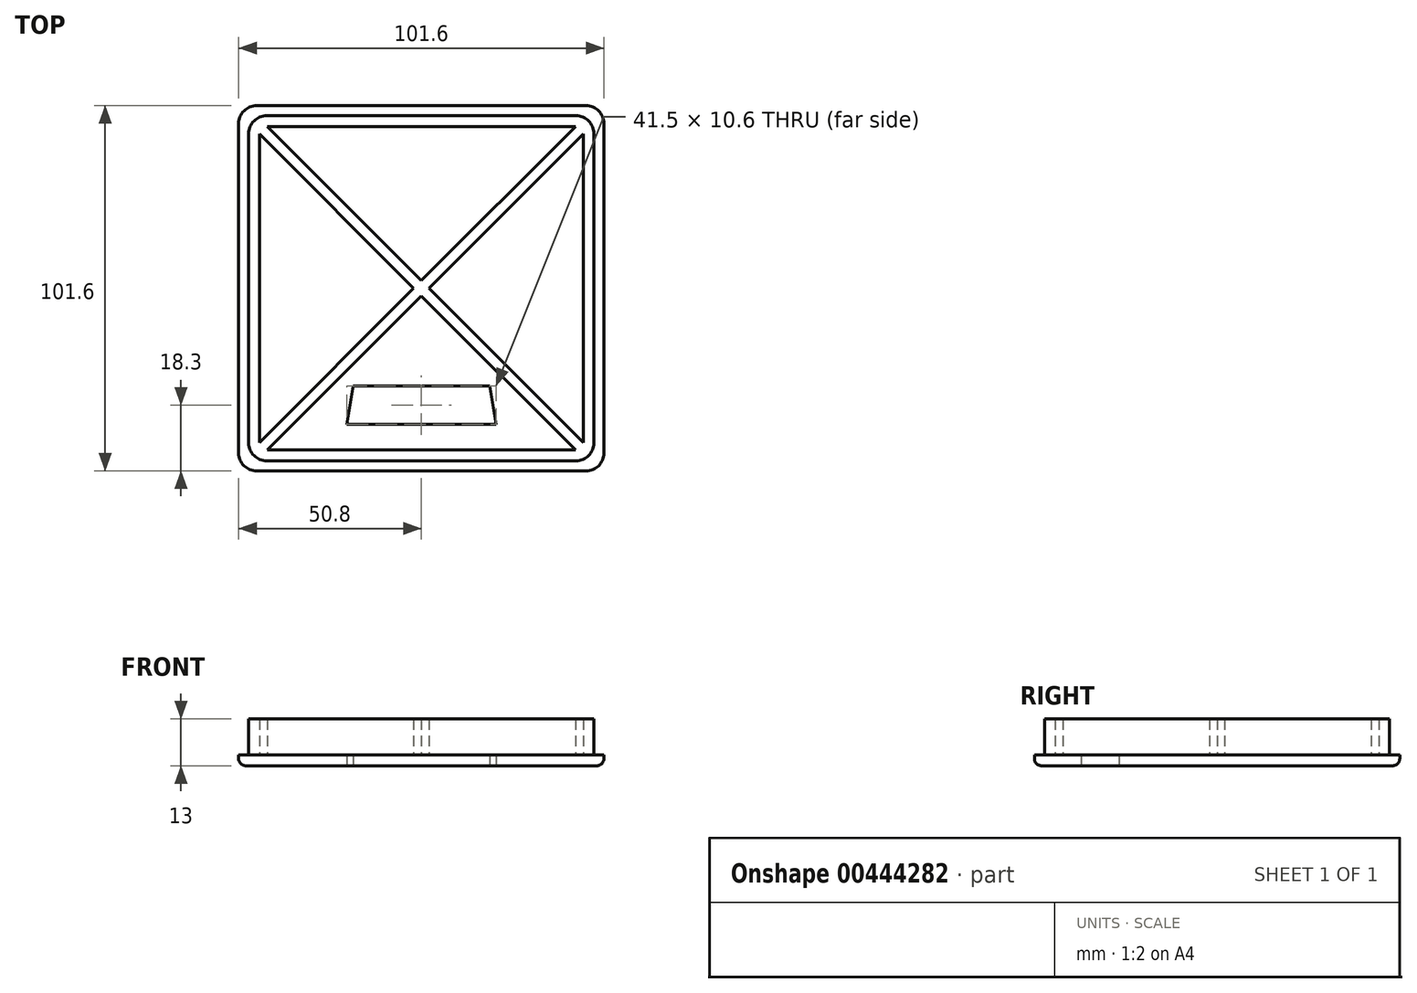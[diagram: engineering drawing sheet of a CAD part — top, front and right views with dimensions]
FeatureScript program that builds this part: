
annotation { "Feature Type Name" : "Feature", "Feature Type Description" : "" }
export const myFeature = defineFeature(function(context is Context, id is Id, definition is map)
    precondition{}
    {
        {
            assignVariable(context, id + "F0", {"name" : "thickness", "anyValue" : 3});
        }
        {
            var Q0;
            Q0=qCreatedBy(makeId("Top.planeOp"),FACE);
            var sketch = newSketch(context, id + "F1", { "sketchPlane" : qUnion([Q0])});
            skLineSegment(sketch, "E0.bottom", {"start": v(45, -45) * mm, "end": v(-45, -45) * mm});
            skLineSegment(sketch, "E0.top", {"start": v(45, 45) * mm, "end": v(-45, 45) * mm});
            skLineSegment(sketch, "E0.left", {"start": v(45, -45) * mm, "end": v(45, 45) * mm});
            skLineSegment(sketch, "E0.right", {"start": v(-45, -45) * mm, "end": v(-45, 45) * mm});
            skPoint(sketch, "E0.middle", {"position": v(0, 0) * mm});
            skLineSegment(sketch, "E1.bottom", {"start": v(-43, 48) * mm, "end": v(43, 48) * mm});
            skLineSegment(sketch, "E1.top", {"start": v(-43, -48) * mm, "end": v(43, -48) * mm});
            skLineSegment(sketch, "E1.left", {"start": v(-48, 43) * mm, "end": v(-48, -43) * mm});
            skLineSegment(sketch, "E1.right", {"start": v(48, 43) * mm, "end": v(48, -43) * mm});
            skLineSegment(sketch, "E2", {"start": v(-45, 45) * mm, "end": v(45, -45) * mm, "construction": true});
            skLineSegment(sketch, "E3", {"start": v(45, 45) * mm, "end": v(-45, -45) * mm, "construction": true});
            skLineSegment(sketch, "E4.bottom", {"start": v(-2.12, 2.12) * mm, "end": v(2.12, 2.12) * mm, "construction": true});
            skLineSegment(sketch, "E4.top", {"start": v(-2.12, -2.12) * mm, "end": v(2.12, -2.12) * mm, "construction": true});
            skLineSegment(sketch, "E4.left", {"start": v(-2.12, 2.12) * mm, "end": v(-2.12, -2.12) * mm, "construction": true});
            skLineSegment(sketch, "E4.right", {"start": v(2.12, 2.12) * mm, "end": v(2.12, -2.12) * mm, "construction": true});
            skPoint(sketch, "E5", {"position": v(2.12, 0) * mm});
            skLineSegment(sketch, "E6", {"start": v(0, 2.12) * mm, "end": v(2.12, 0) * mm, "construction": true});
            skLineSegment(sketch, "E7", {"start": v(-2.12, 0) * mm, "end": v(-45, -42.88) * mm});
            skLineSegment(sketch, "E8", {"start": v(0, -2.12) * mm, "end": v(-42.88, -45) * mm});
            skLineSegment(sketch, "E9", {"start": v(0, -2.12) * mm, "end": v(42.88, -45) * mm});
            skLineSegment(sketch, "E10", {"start": v(2.12, 0) * mm, "end": v(45, -42.88) * mm});
            skLineSegment(sketch, "E11", {"start": v(2.12, 0) * mm, "end": v(45, 42.88) * mm});
            skLineSegment(sketch, "E12", {"start": v(0, 2.12) * mm, "end": v(42.88, 45) * mm});
            skLineSegment(sketch, "E13", {"start": v(0, 2.12) * mm, "end": v(-42.88, 45) * mm});
            skLineSegment(sketch, "E14", {"start": v(-2.12, 0) * mm, "end": v(-45, 42.88) * mm});
            skLineSegment(sketch, "E15.bottom", {"start": v(-45.8, 50.8) * mm, "end": v(45.8, 50.8) * mm});
            skLineSegment(sketch, "E15.top", {"start": v(-45.8, -50.8) * mm, "end": v(45.8, -50.8) * mm});
            skLineSegment(sketch, "E15.left", {"start": v(-50.8, 45.8) * mm, "end": v(-50.8, -45.8) * mm});
            skLineSegment(sketch, "E15.right", {"start": v(50.8, 45.8) * mm, "end": v(50.8, -45.8) * mm});
            skPoint(sketch, "E16.visualSharp", {"position": v(-50.8, 50.8) * mm});
            skArc(sketch, "E16.filletArc", {"start": v(-45.8, 50.8) * mm, "mid": v(-49.34, 49.34) * mm, "end": v(-50.8, 45.8) * mm});
            skPoint(sketch, "E17.visualSharp", {"position": v(50.8, 50.8) * mm});
            skArc(sketch, "E17.filletArc", {"start": v(50.8, 45.8) * mm, "mid": v(49.34, 49.34) * mm, "end": v(45.8, 50.8) * mm});
            skPoint(sketch, "E18.visualSharp", {"position": v(50.8, -50.8) * mm});
            skArc(sketch, "E18.filletArc", {"start": v(45.8, -50.8) * mm, "mid": v(49.34, -49.34) * mm, "end": v(50.8, -45.8) * mm});
            skPoint(sketch, "E19.visualSharp", {"position": v(-50.8, -50.8) * mm});
            skArc(sketch, "E19.filletArc", {"start": v(-50.8, -45.8) * mm, "mid": v(-49.34, -49.34) * mm, "end": v(-45.8, -50.8) * mm});
            skPoint(sketch, "E20.visualSharp", {"position": v(-48, -48) * mm});
            skArc(sketch, "E20.filletArc", {"start": v(-48, -43) * mm, "mid": v(-46.54, -46.54) * mm, "end": v(-43, -48) * mm});
            skPoint(sketch, "E21.visualSharp", {"position": v(48, 48) * mm});
            skArc(sketch, "E21.filletArc", {"start": v(48, 43) * mm, "mid": v(46.54, 46.54) * mm, "end": v(43, 48) * mm});
            skPoint(sketch, "E22.visualSharp", {"position": v(48, -48) * mm});
            skArc(sketch, "E22.filletArc", {"start": v(43, -48) * mm, "mid": v(46.54, -46.54) * mm, "end": v(48, -43) * mm});
            skPoint(sketch, "E23.visualSharp", {"position": v(-48, 48) * mm});
            skArc(sketch, "E23.filletArc", {"start": v(-43, 48) * mm, "mid": v(-46.54, 46.54) * mm, "end": v(-48, 43) * mm});
            skSolve(sketch);
        }
        {
            var Q0;
            Q0 = qSketchRegion(id + "F1", true);
            var Q1;
            Q1=makeQuery(id+"F1.imprint","IMPRINT",FACE,{"disambiguationData":[TD([[makeQuery(id+"F1.imprint","IMPRINT",EDGE,{"derivedFrom":sQuery(id+"F1.wireOp",EDGE,"E1.bottom")}),-1.0]])]});
            var Q2;
            {var subQ0=sQuery(id+"F1.wireOp",EDGE,"E7");Q2=makeQuery(id+"F1.imprint","IMPRINT",FACE,{"disambiguationData":[TD([[makeQuery(id+"F1.imprint","IMPRINT",EDGE,{"derivedFrom":subQ0}),-1.0]])]});}
            var Q3;
            {var subQ0=sQuery(id+"F1.wireOp",EDGE,"E12");Q3=makeQuery(id+"F1.imprint","IMPRINT",FACE,{"disambiguationData":[TD([[makeQuery(id+"F1.imprint","IMPRINT",EDGE,{"derivedFrom":subQ0}),1.0]])]});}
            var Q4;
            {var subQ0=sQuery(id+"F1.wireOp",EDGE,"E10");Q4=makeQuery(id+"F1.imprint","IMPRINT",FACE,{"disambiguationData":[TD([[makeQuery(id+"F1.imprint","IMPRINT",EDGE,{"derivedFrom":subQ0}),1.0]])]});}
            var Q5;
            {var subQ0=sQuery(id+"F1.wireOp",EDGE,"E8");Q5=makeQuery(id+"F1.imprint","IMPRINT",FACE,{"disambiguationData":[TD([[makeQuery(id+"F1.imprint","IMPRINT",EDGE,{"derivedFrom":subQ0}),1.0]])]});}
            var Q6;
            {var subQ3=sQuery(id+"F1.wireOp",EDGE,"E7");Q6=makeQuery(id+"F1.imprint","IMPRINT",FACE,{"disambiguationData":[TD([[makeQuery(id+"F1.imprint","IMPRINT",EDGE,{"derivedFrom":subQ3}),1.0]])]});}
            extrude(context, id + "F2", {"entities" : qUnion([Q0, Q1, Q2, Q3, Q4, Q5, Q6]), "oppositeDirection" : true, "depth" : (getVariable(context, 'thickness')) * mm});
        }
        {
            var Q0;
            {var subQ3=sQuery(id+"F1.wireOp",EDGE,"E7");Q0=makeQuery(id+"F1.imprint","IMPRINT",FACE,{"disambiguationData":[TD([[makeQuery(id+"F1.imprint","IMPRINT",EDGE,{"derivedFrom":subQ3}),1.0]])]});}
            var Q1;
            Q1=makeQuery(id+"F1.imprint","IMPRINT",FACE,{"disambiguationData":[TD([[makeQuery(id+"F1.imprint","IMPRINT",EDGE,{"derivedFrom":sQuery(id+"F1.wireOp",EDGE,"E1.bottom")}),-1.0]])]});
            extrude(context, id + "F3", {"entities" : qUnion([Q0, Q1]), "operationType" : NewBodyOperationType.ADD, "depth" : 10 * mm});
        }
        {
            var Q0;
            Q0=makeQuery(id+"F2.opExtrude","CAP_FACE",FACE,{"disambiguationData":[OSD([sQuery(id+"F1.wireOp",EDGE,"E15.bottom"),sQuery(id+"F1.wireOp",EDGE,"E15.top"),sQuery(id+"F1.wireOp",EDGE,"E15.left"),sQuery(id+"F1.wireOp",EDGE,"E15.right"),sQuery(id+"F1.wireOp",EDGE,"E16.filletArc"),sQuery(id+"F1.wireOp",EDGE,"E17.filletArc"),sQuery(id+"F1.wireOp",EDGE,"E18.filletArc"),sQuery(id+"F1.wireOp",EDGE,"E19.filletArc")])],"isStart":false});
            fillet(context, id + "F4", {"entities" : qUnion([Q0]), "radius" : 2 * mm, "tangentPropagation" : true, "allowEdgeOverflow" : false});
        }
        {
            var Q0;
            Q0=makeQuery(id+"F2.opExtrude","CAP_FACE",FACE,{"disambiguationData":[OSD([sQuery(id+"F1.wireOp",EDGE,"E15.bottom"),sQuery(id+"F1.wireOp",EDGE,"E15.top"),sQuery(id+"F1.wireOp",EDGE,"E15.left"),sQuery(id+"F1.wireOp",EDGE,"E15.right"),sQuery(id+"F1.wireOp",EDGE,"E16.filletArc"),sQuery(id+"F1.wireOp",EDGE,"E17.filletArc"),sQuery(id+"F1.wireOp",EDGE,"E18.filletArc"),sQuery(id+"F1.wireOp",EDGE,"E19.filletArc")])],"isStart":false});
            var sketch = newSketch(context, id + "F5", { "sketchPlane" : qUnion([Q0])});
            skLineSegment(sketch, "E24", {"start": v(-20.75, 37.8) * mm, "end": v(20.75, 37.8) * mm});
            skLineSegment(sketch, "E25", {"start": v(20.75, 37.8) * mm, "end": v(19, 27.2) * mm});
            skLineSegment(sketch, "E26", {"start": v(19, 27.2) * mm, "end": v(-19, 27.2) * mm});
            skLineSegment(sketch, "E27", {"start": v(-19, 27.2) * mm, "end": v(-20.75, 37.8) * mm});
            skPoint(sketch, "E28", {"position": v(0, 37.8) * mm});
            skPoint(sketch, "E29", {"position": v(0, 27.2) * mm});
            skSolve(sketch);
        }
        {
            var Q0;
            Q0=makeQuery(id+"F5.imprint","IMPRINT",FACE,{"disambiguationData":[TD([[makeQuery(id+"F5.imprint","IMPRINT",EDGE,{"derivedFrom":sQuery(id+"F5.wireOp",EDGE,"E24")}),-1.0]])]});
            extrude(context, id + "F6", {"entities" : qUnion([Q0]), "operationType" : NewBodyOperationType.REMOVE, "oppositeDirection" : true, "depth" : 4.4 * mm});
        }
    });
